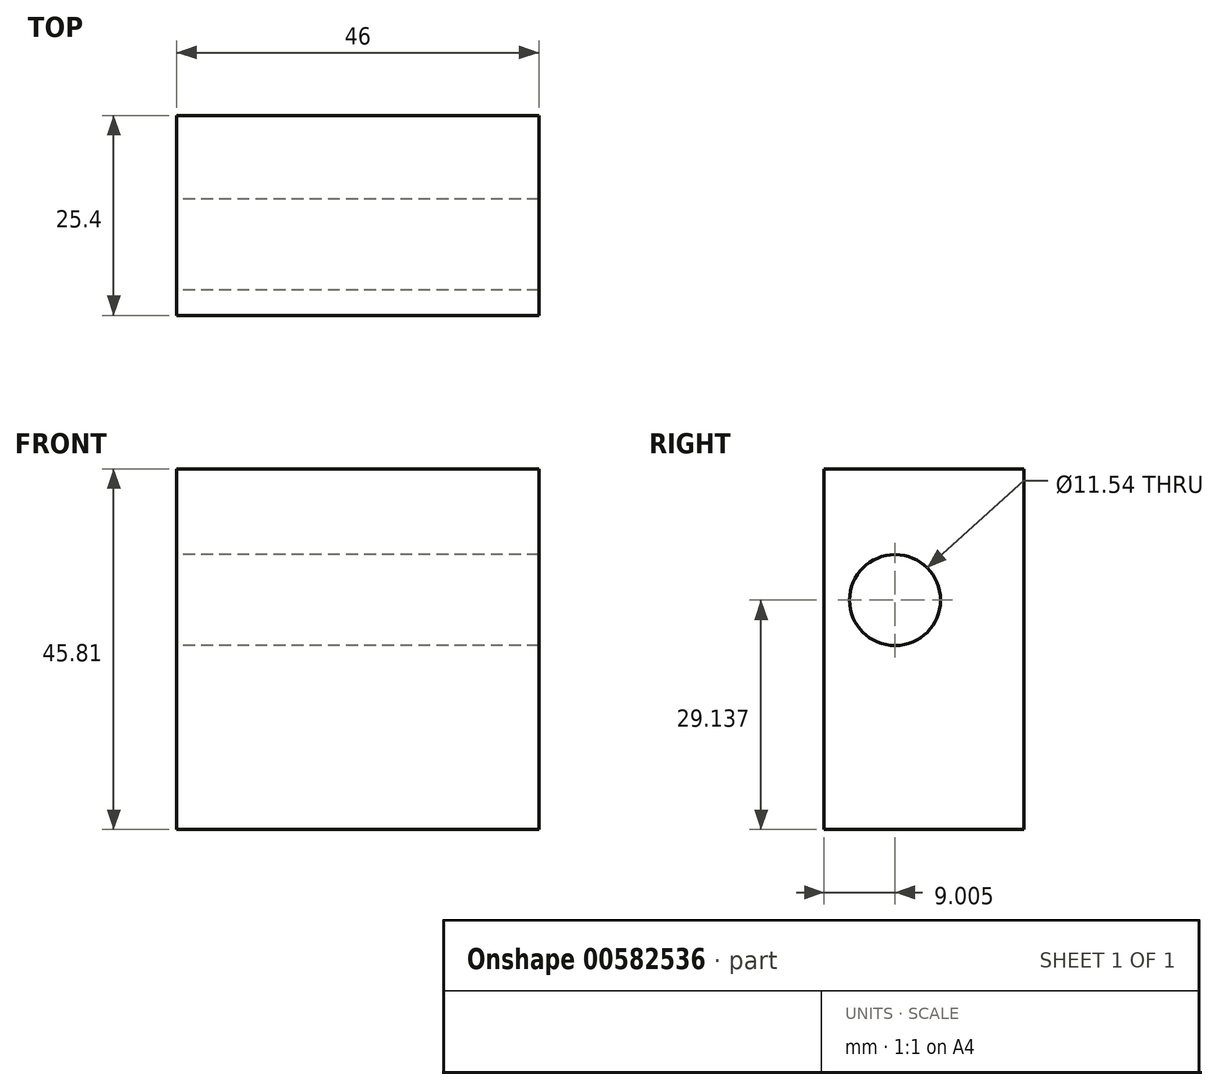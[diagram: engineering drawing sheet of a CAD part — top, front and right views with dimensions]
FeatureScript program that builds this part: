
annotation { "Feature Type Name" : "Feature", "Feature Type Description" : "" }
export const myFeature = defineFeature(function(context is Context, id is Id, definition is map)
    precondition{}
    {
        {
            var Q0;
            Q0=qCreatedBy(makeId("Front.planeOp"),FACE);
            var sketch = newSketch(context, id + "F0", { "sketchPlane" : qUnion([Q0])});
            skLineSegment(sketch, "E0.bottom", {"start": v(0, 0) * mm, "end": v(46, 0) * mm});
            skLineSegment(sketch, "E0.top", {"start": v(0, 45.81) * mm, "end": v(46, 45.81) * mm});
            skLineSegment(sketch, "E0.left", {"start": v(0, 0) * mm, "end": v(0, 45.81) * mm});
            skLineSegment(sketch, "E0.right", {"start": v(46, 0) * mm, "end": v(46, 45.81) * mm});
            skSolve(sketch);
        }
        {
            var Q0;
            Q0=makeQuery(id+"F0.imprint","IMPRINT",FACE,{"disambiguationData":[TD([[makeQuery(id+"F0.imprint","IMPRINT",EDGE,{"derivedFrom":sQuery(id+"F0.wireOp",EDGE,"E0.bottom")}),1.0]])]});
            extrude(context, id + "F1", {"entities" : qUnion([Q0]), "depth" : 25.4 * mm, "offsetDistance" : 25.4 * mm});
        }
        {
            var Q0;
            Q0=qCreatedBy(makeId("Right.planeOp"),FACE);
            var sketch = newSketch(context, id + "F2", { "sketchPlane" : qUnion([Q0])});
            skCircle(sketch, "E1", {"center": v(-16.4, 29.14) * mm, "radius": 5.77 * mm});
            skSolve(sketch);
        }
        {
            var Q0;
            Q0 = qSketchRegion(id + "F2", true);
            extrude(context, id + "F3", {"entities" : qUnion([Q0]), "operationType" : NewBodyOperationType.REMOVE, "endBound" : BoundingType.THROUGH_ALL, "depth" : 25.4 * mm, "offsetDistance" : 25.4 * mm});
        }
    });
